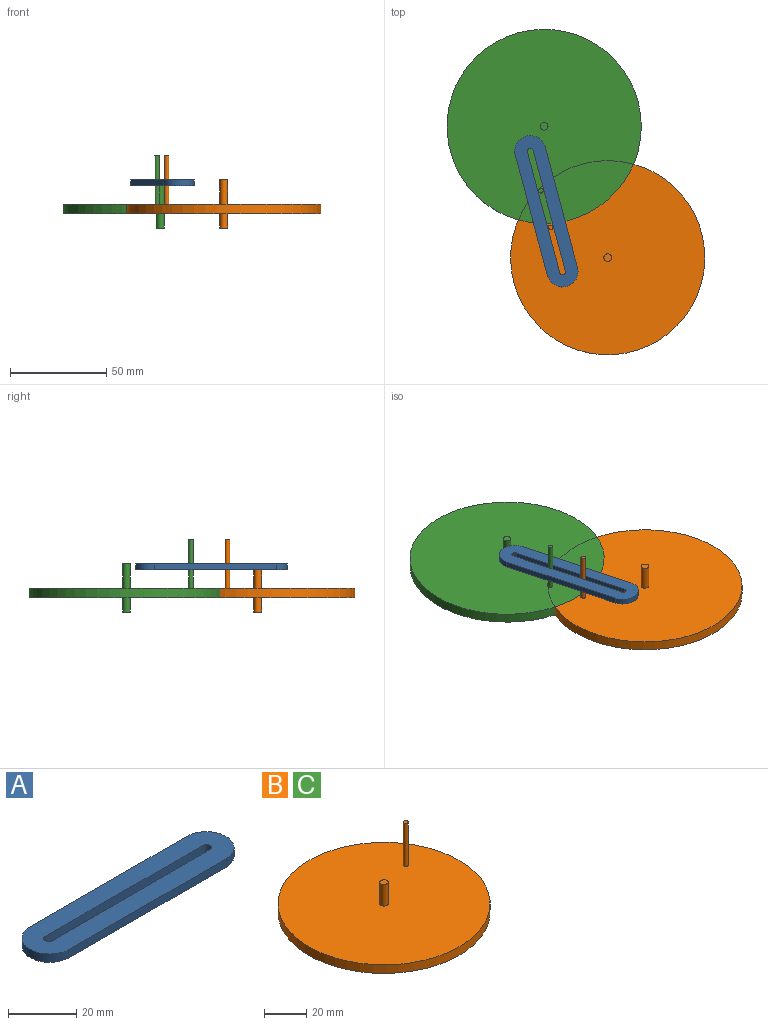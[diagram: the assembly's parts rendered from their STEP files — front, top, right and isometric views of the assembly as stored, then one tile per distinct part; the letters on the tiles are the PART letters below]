
ASSEMBLY  parts=3 mates=2
PART A: 11 faces, bbox 80.9x16.2x3 mm
  f0: plane 65.25x3mm, normal (0,-1,0), area 195.7mm2, adj f1,f8,f9,f10
  f1: cylinder r=8.09mm len=16.17mm, axis (0,0,-1), area 75.2mm2, adj f0,f2,f9,f10
  f2: plane 65.25x3mm, normal (0,1,0), area 195.7mm2, adj f1,f8,f9,f10
  f3: plane 65.11x3mm, normal (0,1,0), area 195.3mm2, adj f4,f7,f9,f10
  f4: plane 3x0.01mm, normal (1,0,0), area 0mm2, adj f3,f5,f9,f10
  f5: cylinder r=1.51mm len=3.02mm, axis (0,0,-1), area 14.3mm2, adj f4,f6,f9,f10
  f6: plane 64.74x3mm, normal (0,-1,0), area 194.2mm2, adj f5,f7,f9,f10
  f7: cylinder r=1.52mm len=3.04mm, axis (0,0,-1), area 15.2mm2, adj f3,f6,f9,f10
  f8: cylinder r=8.09mm len=16.17mm, axis (0,0,-1), area 74.3mm2, adj f0,f2,f9,f10
  f9: plane 80.92x16.17mm, normal (0,0,1), area 1048.8mm2, adj f0,f1,f2,f3,f4,f5,f6,f7
  f10: plane 80.92x16.17mm, normal (0,0,-1), area 1048.8mm2, adj f0,f1,f2,f3,f4,f5,f6,f7
PART B: 9 faces, bbox 101x101x37.5 mm
  f0: cylinder r=50.5mm len=101mm, axis (0,0,1), area 1586.5mm2, adj f1,f2
  f1: plane 101x101mm, normal (0,0,-1), area 7998.9mm2, adj f0,f7
  f2: plane 101x101mm, normal (0,0,1), area 7994.4mm2, adj f0,f3,f6
  f3: cylinder r=1.2mm len=25mm, axis (0,0,-1), area 188.5mm2, adj f2,f4
  f4: plane 2.4x2.4mm, normal (0,0,1), area 4.5mm2, adj f3
  f5: plane 4x4mm, normal (0,0,1), area 12.6mm2, adj f6
  f6: cylinder r=2mm len=12.5mm, axis (0,0,-1), area 157.1mm2, adj f2,f5
  f7: cylinder r=2mm len=7.5mm, axis (0,0,-1), area 94.2mm2, adj f1,f8
  f8: plane 4x4mm, normal (0,0,-1), area 12.6mm2, adj f7
PART C: same geometry as B
PLACE A rot(axis=(0,0,1),105deg) t=(114.56,-54.48,28.26)mm
PLACE B rot(axis=(0,0,1),125deg) t=(143.95,-62.73,18.76)mm
PLACE C rot(axis=(0,0,-1),120deg) t=(110.9,5.58,18.76)mm
MATE pin_slot C.f3 <-> A.f1  axis (0,0,-1) through (109.18,-27.95,31.26)mm
MATE pin_slot B.f3 <-> A.f9  axis (0,0,-1) through (114.29,-47.01,31.26)mm
